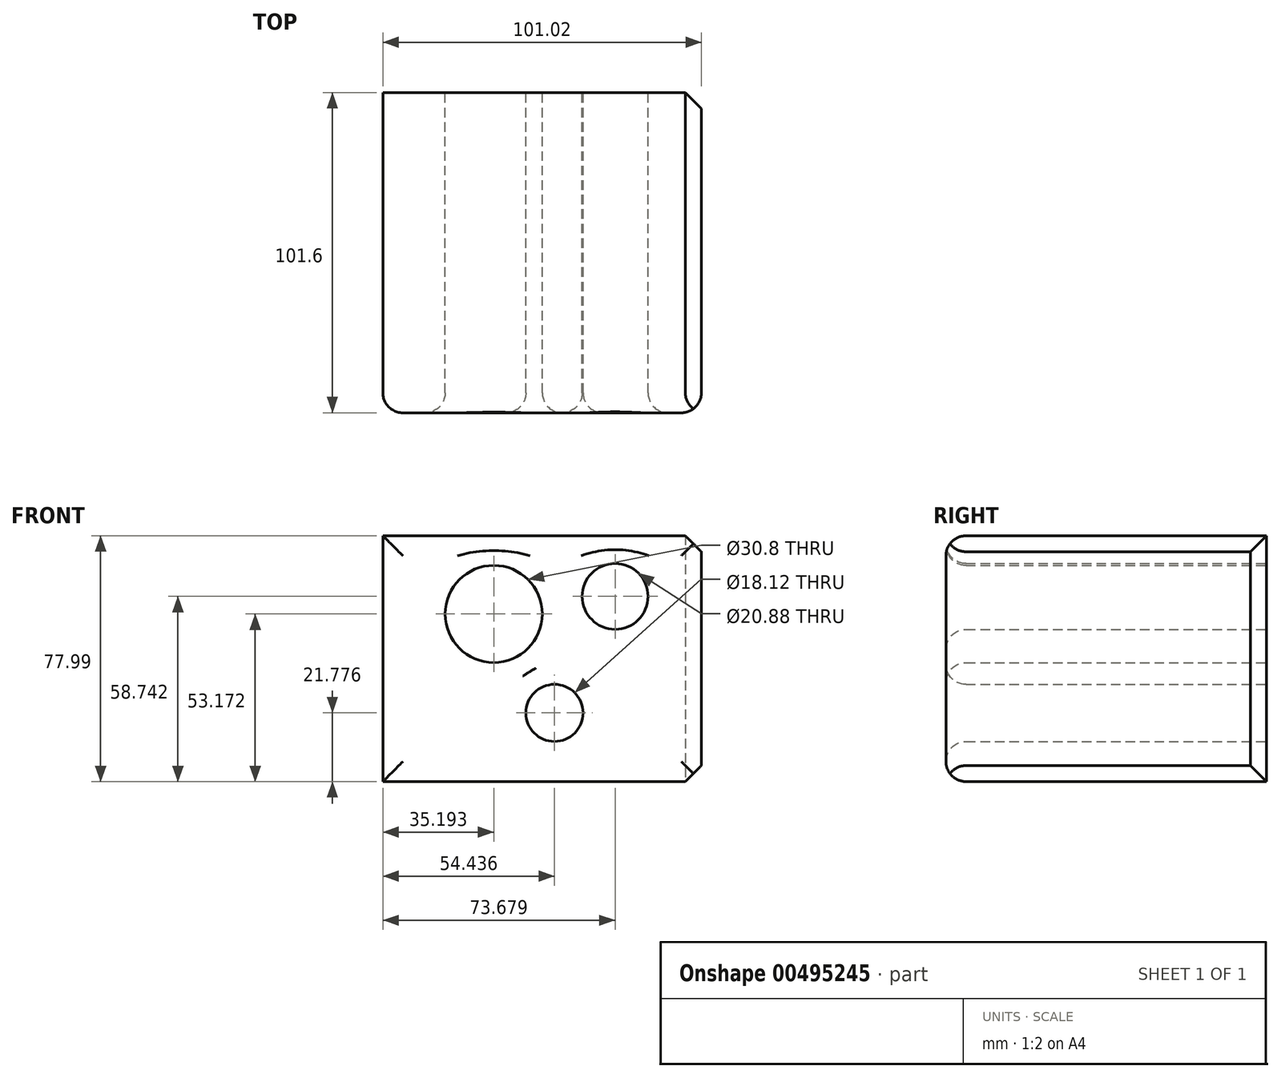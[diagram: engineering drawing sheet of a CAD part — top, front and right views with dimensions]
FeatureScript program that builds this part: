
annotation { "Feature Type Name" : "Feature", "Feature Type Description" : "" }
export const myFeature = defineFeature(function(context is Context, id is Id, definition is map)
    precondition{}
    {
        {
            var Q0;
            Q0=qCreatedBy(makeId("Front.planeOp"),FACE);
            var sketch = newSketch(context, id + "F0", { "sketchPlane" : qUnion([Q0])});
            skLineSegment(sketch, "E0.bottom", {"start": v(-65.83, 45.58) * mm, "end": v(35.2, 45.58) * mm});
            skLineSegment(sketch, "E0.top", {"start": v(-65.83, -32.4) * mm, "end": v(35.2, -32.4) * mm});
            skLineSegment(sketch, "E0.left", {"start": v(-65.83, 45.58) * mm, "end": v(-65.83, -32.4) * mm});
            skLineSegment(sketch, "E0.right", {"start": v(35.2, 45.58) * mm, "end": v(35.2, -32.4) * mm});
            skCircle(sketch, "E1", {"center": v(-30.64, 20.76) * mm, "radius": 15.4 * mm});
            skCircle(sketch, "E2", {"center": v(-11.4, -10.63) * mm, "radius": 9.06 * mm});
            skCircle(sketch, "E3", {"center": v(7.85, 26.33) * mm, "radius": 10.44 * mm});
            skSolve(sketch);
        }
        {
            var Q0;
            Q0=makeQuery(id+"F0.imprint","IMPRINT",FACE,{"disambiguationData":[TD([[makeQuery(id+"F0.imprint","IMPRINT",EDGE,{"derivedFrom":sQuery(id+"F0.wireOp",EDGE,"E0.bottom")}),-1.0]])]});
            extrude(context, id + "F1", {"entities" : qUnion([Q0]), "depth" : 101.6 * mm});
        }
        {
            var Q0;
            Q0=makeQuery(id+"F1.opExtrude","CAP_FACE",FACE,{"disambiguationData":[OSD([sQuery(id+"F0.wireOp",EDGE,"E0.bottom"),sQuery(id+"F0.wireOp",EDGE,"E0.top"),sQuery(id+"F0.wireOp",EDGE,"E0.left"),sQuery(id+"F0.wireOp",EDGE,"E0.right"),sQuery(id+"F0.wireOp",EDGE,"E1"),sQuery(id+"F0.wireOp",EDGE,"E2"),sQuery(id+"F0.wireOp",EDGE,"E3")])],"isStart":false});
            fillet(context, id + "F2", {"entities" : qUnion([Q0]), "radius" : 6.35 * mm, "tangentPropagation" : true, "allowEdgeOverflow" : false});
        }
        {
            var Q0;
            Q0=makeQuery(id+"F1.opExtrude","SWEPT_FACE",FACE,{"disambiguationData":[OSD([sQuery(id+"F0.wireOp",EDGE,"E0.right")])]});
            var Q1;
            {var subQ0=sQuery(id+"F0.wireOp",EDGE,"E0.right");Q1=makeQuery(id+"F2.opFillet","BLEND_EDGE",EDGE,{"blendedFrom":[makeQuery(id+"F1.opExtrude","CAP_EDGE",EDGE,{"disambiguationData":[OSD([subQ0])],"isStart":false}),makeQuery(id+"F1.opExtrude","SWEPT_FACE",FACE,{"disambiguationData":[OSD([subQ0])]})],"blendedInto":[makeQuery(id+"F1.opExtrude","SWEPT_FACE",FACE,{"disambiguationData":[OSD([subQ0])]})]});}
            var Q2;
            Q2=makeQuery(id+"F1.opExtrude","CAP_EDGE",EDGE,{"disambiguationData":[OSD([sQuery(id+"F0.wireOp",EDGE,"E0.right")])],"isStart":true});
            var Q3;
            Q3=makeQuery(id+"F1.opExtrude","SWEPT_EDGE",EDGE,{"disambiguationData":[OSD([sQuery(id+"F0.wireOp",EDGE,"E0.bottom"),sQuery(id+"F0.wireOp",EDGE,"E0.right")])]});
            var Q4;
            Q4=makeQuery(id+"F1.opExtrude","SWEPT_EDGE",EDGE,{"disambiguationData":[OSD([sQuery(id+"F0.wireOp",EDGE,"E0.top"),sQuery(id+"F0.wireOp",EDGE,"E0.right")])]});
            chamfer(context, id + "F3", {"entities" : qUnion([Q0, Q1, Q2, Q3, Q4]), "width" : 5.08 * mm, "tangentPropagation" : true});
        }
    });
